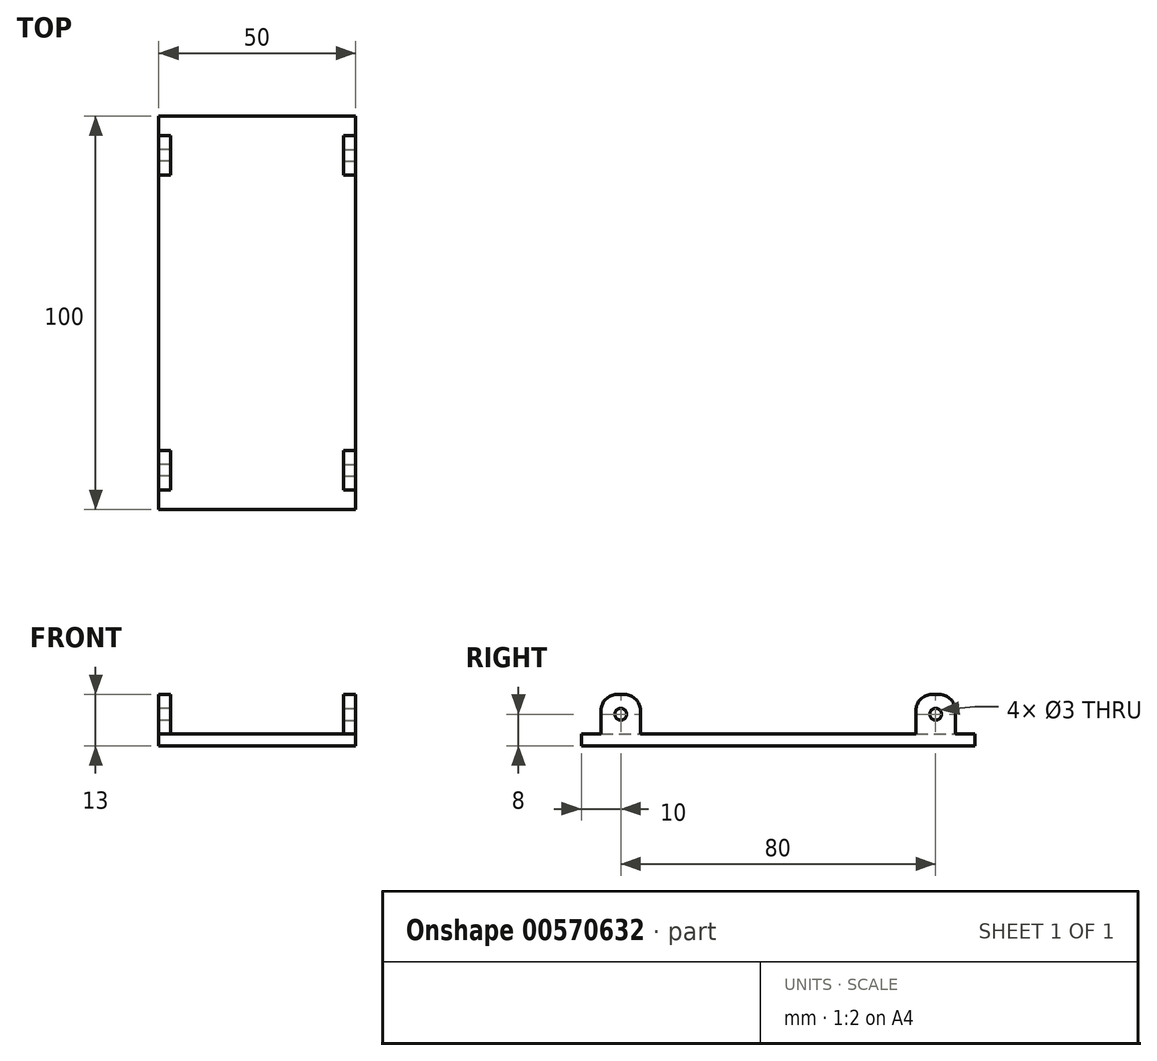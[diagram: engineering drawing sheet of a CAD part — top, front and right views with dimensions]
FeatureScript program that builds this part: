
annotation { "Feature Type Name" : "Feature", "Feature Type Description" : "" }
export const myFeature = defineFeature(function(context is Context, id is Id, definition is map)
    precondition{}
    {
        {
            var Q0;
            Q0=qCreatedBy(makeId("Top.planeOp"),FACE);
            var sketch = newSketch(context, id + "F0", { "sketchPlane" : qUnion([Q0])});
            skLineSegment(sketch, "E0.bottom", {"start": v(12.5, -50) * mm, "end": v(-12.5, -50) * mm});
            skLineSegment(sketch, "E0.top", {"start": v(12.5, 50) * mm, "end": v(-12.5, 50) * mm});
            skLineSegment(sketch, "E0.left", {"start": v(12.5, -50) * mm, "end": v(12.5, 50) * mm});
            skLineSegment(sketch, "E0.right", {"start": v(-12.5, -50) * mm, "end": v(-12.5, 50) * mm});
            skPoint(sketch, "E0.middle", {"position": v(0, 0) * mm});
            skSolve(sketch);
        }
        {
            var Q0;
            Q0 = qSketchRegion(id + "F0", true);
            extrude(context, id + "F1", {"entities" : qUnion([Q0]), "depth" : 3 * mm, "offsetDistance" : 25 * mm});
        }
        {
            var Q0;
            Q0=makeQuery(id+"F1.opExtrude","SWEPT_FACE",FACE,{"disambiguationData":[OSD([sQuery(id+"F0.wireOp",EDGE,"E0.left")])]});
            var sketch = newSketch(context, id + "F2", { "sketchPlane" : qUnion([Q0])});
            skLineSegment(sketch, "E1.bottom", {"start": v(-45, 3) * mm, "end": v(-35, 3) * mm});
            skLineSegment(sketch, "E1.top", {"start": v(-41, 13) * mm, "end": v(-39, 13) * mm});
            skLineSegment(sketch, "E1.left", {"start": v(-45, 3) * mm, "end": v(-45, 9) * mm});
            skLineSegment(sketch, "E1.right", {"start": v(-35, 3) * mm, "end": v(-35, 9) * mm});
            skLineSegment(sketch, "E2.MirrorCS", {"start": v(35, 3) * mm, "end": v(35, 9) * mm});
            skLineSegment(sketch, "E3.MirrorCS", {"start": v(41, 13) * mm, "end": v(39, 13) * mm});
            skLineSegment(sketch, "E4.MirrorCS", {"start": v(45, 3) * mm, "end": v(45, 9) * mm});
            skCircle(sketch, "E5", {"center": v(-40, 8) * mm, "radius": 1.5 * mm});
            skPoint(sketch, "E5.centerSnap0", {"position": v(-40, 3) * mm});
            skCircle(sketch, "E6.MirrorC", {"center": v(40, 8) * mm, "radius": 1.5 * mm});
            skPoint(sketch, "E7.visualSharp", {"position": v(-45, 13) * mm});
            skArc(sketch, "E7.filletArc", {"start": v(-41, 13) * mm, "mid": v(-43.83, 11.83) * mm, "end": v(-45, 9) * mm});
            skPoint(sketch, "E8.visualSharp", {"position": v(-35, 13) * mm});
            skArc(sketch, "E8.filletArc", {"start": v(-35, 9) * mm, "mid": v(-36.17, 11.83) * mm, "end": v(-39, 13) * mm});
            skPoint(sketch, "E9.visualSharp", {"position": v(35, 13) * mm});
            skArc(sketch, "E9.filletArc", {"start": v(39, 13) * mm, "mid": v(36.17, 11.83) * mm, "end": v(35, 9) * mm});
            skPoint(sketch, "E10.visualSharp", {"position": v(45, 13) * mm});
            skArc(sketch, "E10.filletArc", {"start": v(45, 9) * mm, "mid": v(43.83, 11.83) * mm, "end": v(41, 13) * mm});
            skSolve(sketch);
        }
        {
            var Q0;
            {var subQ0=sQuery(id+"F2.wireOp",EDGE,"E2.MirrorCS");Q0=makeQuery(id+"F2.imprint","IMPRINT",FACE,{"disambiguationData":[TD([[makeQuery(id+"F2.imprint","IMPRINT",EDGE,{"derivedFrom":subQ0}),-1.0]])]});}
            var Q1;
            Q1=makeQuery(id+"F2.imprint","IMPRINT",FACE,{"disambiguationData":[TD([[makeQuery(id+"F2.imprint","IMPRINT",EDGE,{"derivedFrom":sQuery(id+"F2.wireOp",EDGE,"E1.bottom")}),1.0]])]});
            extrude(context, id + "F3", {"entities" : qUnion([Q0, Q1]), "operationType" : NewBodyOperationType.ADD, "oppositeDirection" : true, "depth" : 3 * mm, "offsetDistance" : 25 * mm});
        }
        {
            var Q0;
            Q0=makeQuery(id+"F1.opExtrude","SWEPT_BODY",BODY,{"disambiguationData":[OSD([sQuery(id+"F0.wireOp",EDGE,"E0.bottom"),sQuery(id+"F0.wireOp",EDGE,"E0.top"),sQuery(id+"F0.wireOp",EDGE,"E0.left"),sQuery(id+"F0.wireOp",EDGE,"E0.right")])]});
            var Q1;
            Q1=makeQuery(id+"F1.opExtrude","SWEPT_FACE",FACE,{"disambiguationData":[OSD([sQuery(id+"F0.wireOp",EDGE,"E0.right")])]});
            mirror(context, id + "F4", {"operationType" : NewBodyOperationType.ADD, "entities" : qUnion([Q0]), "mirrorPlane" : qUnion([Q1])});
        }
    });
